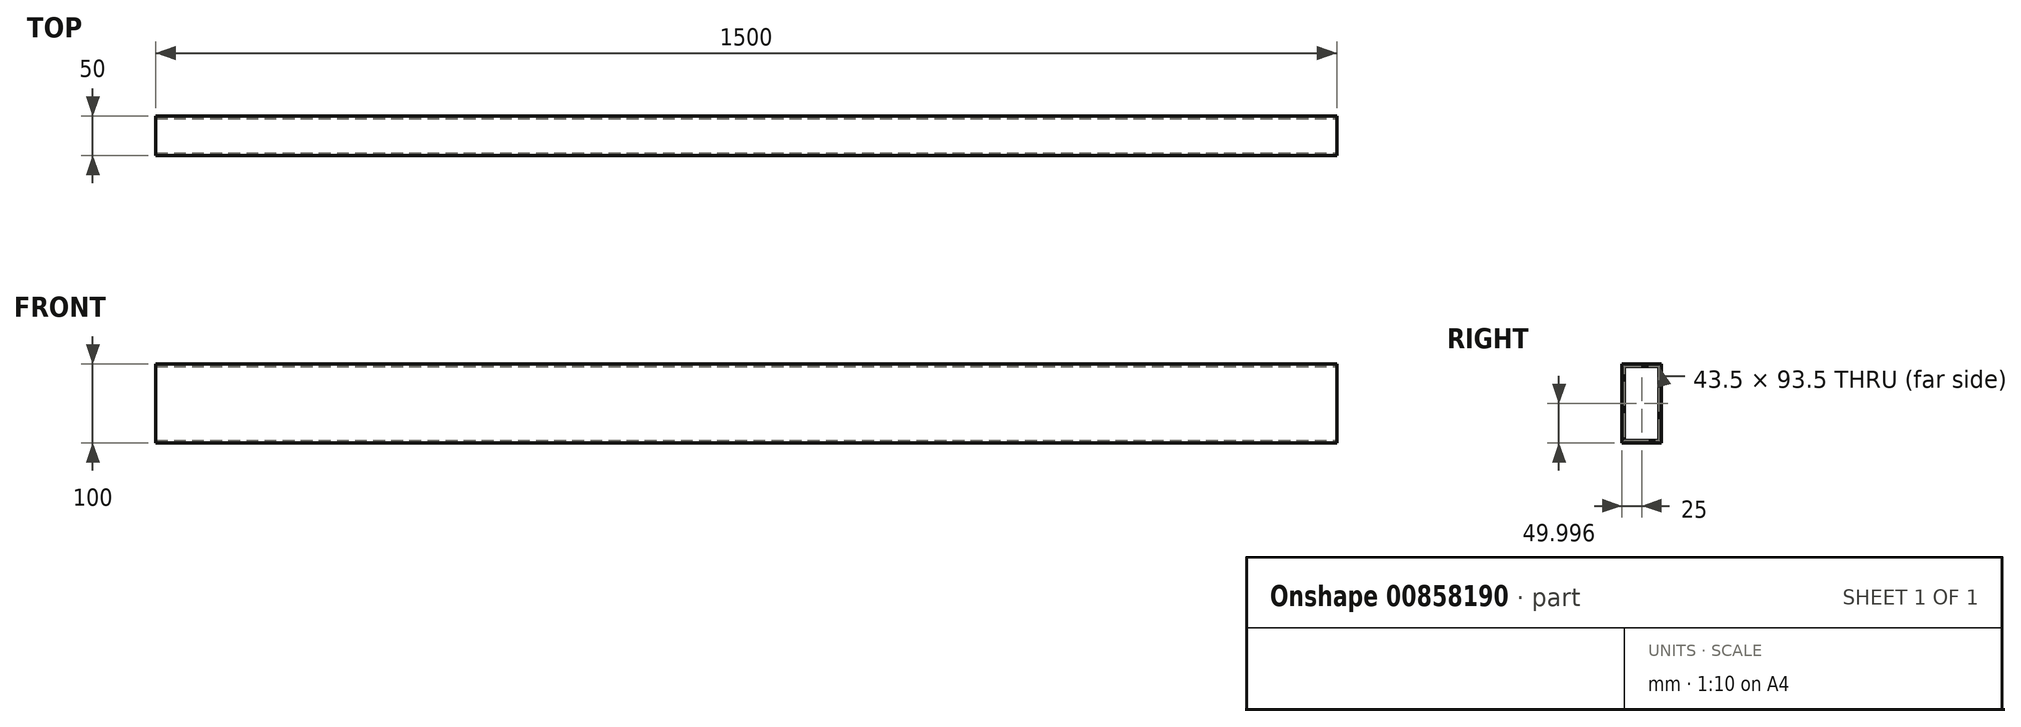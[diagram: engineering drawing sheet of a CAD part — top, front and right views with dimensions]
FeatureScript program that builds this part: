
annotation { "Feature Type Name" : "Feature", "Feature Type Description" : "" }
export const myFeature = defineFeature(function(context is Context, id is Id, definition is map)
    precondition{}
    {
        {
            var Q0;
            Q0=qCreatedBy(makeId("Front.planeOp"),FACE);
            var sketch = newSketch(context, id + "F0", { "sketchPlane" : qUnion([Q0])});
            skLineSegment(sketch, "E0.bottom", {"start": v(-740.9, 46.06) * mm, "end": v(759.1, 46.06) * mm});
            skLineSegment(sketch, "E0.top", {"start": v(-740.9, -53.94) * mm, "end": v(759.1, -53.94) * mm});
            skLineSegment(sketch, "E0.left", {"start": v(-740.9, 46.06) * mm, "end": v(-740.9, -53.94) * mm});
            skLineSegment(sketch, "E0.right", {"start": v(759.1, 46.06) * mm, "end": v(759.1, -53.94) * mm});
            skSolve(sketch);
        }
        {
            var Q0;
            Q0=makeQuery(id+"F0.imprint","IMPRINT",FACE,{"disambiguationData":[TD([[makeQuery(id+"F0.imprint","IMPRINT",EDGE,{"derivedFrom":sQuery(id+"F0.wireOp",EDGE,"E0.bottom")}),-1.0]])]});
            extrude(context, id + "F1", {"entities" : qUnion([Q0]), "depth" : 50 * mm, "offsetDistance" : 25 * mm});
        }
        {
            var Q0;
            Q0=makeQuery(id+"F1.opExtrude","SWEPT_FACE",FACE,{"disambiguationData":[OSD([sQuery(id+"F0.wireOp",EDGE,"E0.right")])]});
            shell(context, id + "F2", {"entities" : qUnion([Q0]), "thickness" : 3.25 * mm});
        }
        {
            var Q0;
            Q0=makeQuery(id+"F2.opShell","OFFSET_FACE",FACE,{"disambiguationData":[OSD([sQuery(id+"F0.wireOp",EDGE,"E0.left")])]});
            extrude(context, id + "F3", {"entities" : qUnion([Q0]), "operationType" : NewBodyOperationType.REMOVE, "oppositeDirection" : true, "depth" : 25 * mm, "offsetDistance" : 25 * mm, "hasSecondDirection" : true, "secondDirectionOppositeDirection" : false, "secondDirectionDepth" : 25 * mm});
        }
    });
